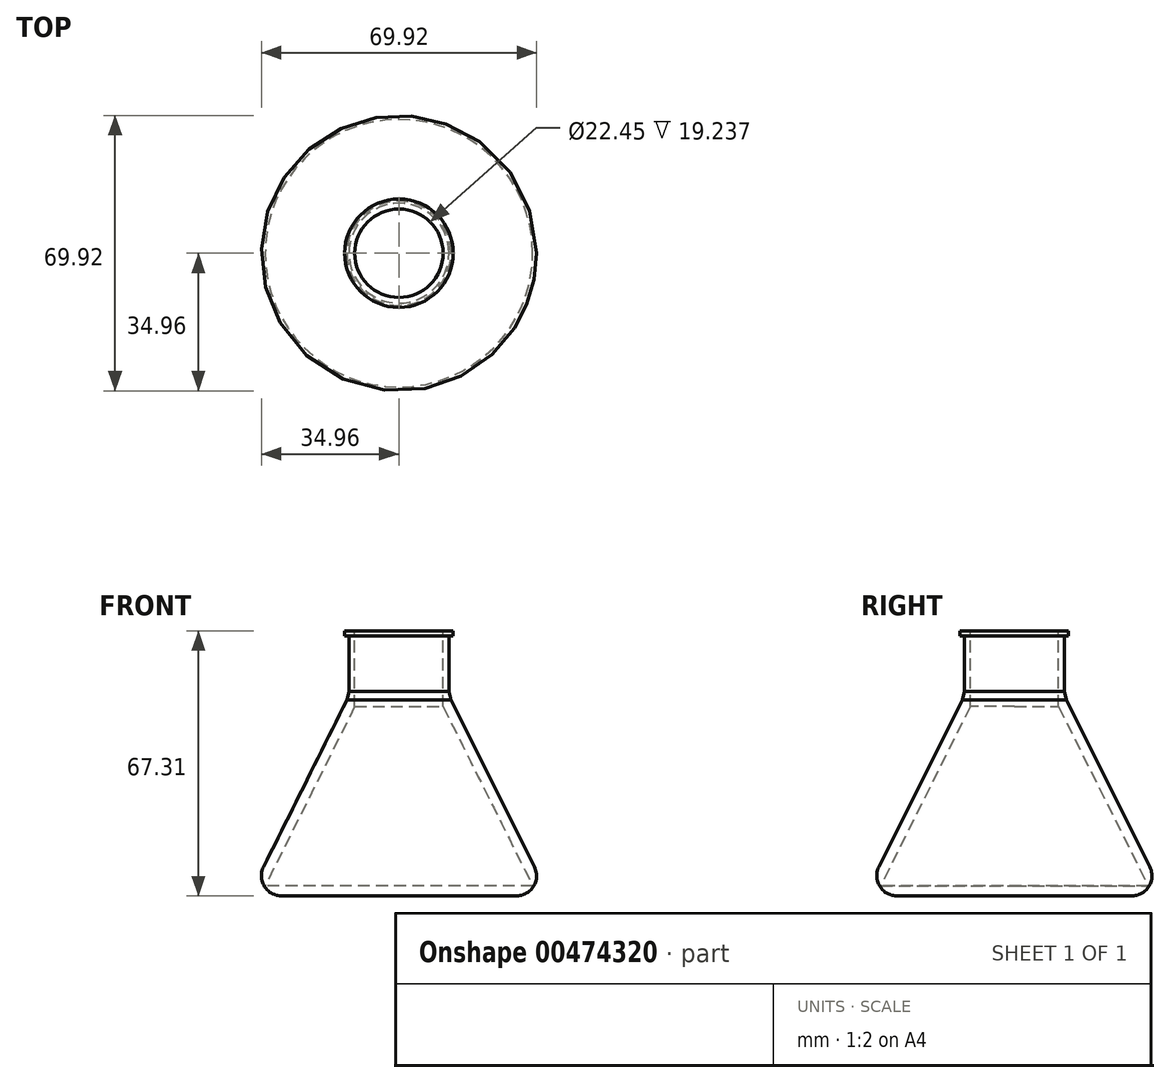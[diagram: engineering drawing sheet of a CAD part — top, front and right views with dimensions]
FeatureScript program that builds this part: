
annotation { "Feature Type Name" : "Feature", "Feature Type Description" : "" }
export const myFeature = defineFeature(function(context is Context, id is Id, definition is map)
    precondition{}
    {
        {
            var Q0;
            Q0=qCreatedBy(makeId("Top.planeOp"),FACE);
            var sketch = newSketch(context, id + "F0", { "sketchPlane" : qUnion([Q0])});
            skCircle(sketch, "E0", {"center": v(0, 0) * mm, "radius": 38.1 * mm});
            skSolve(sketch);
        }
        {
            var Q0;
            Q0=qCreatedBy(makeId("Top.planeOp"),FACE);
            cPlane(context, id + "F1", {"entities" : qUnion([Q0]), "cplaneType" : CPlaneType.OFFSET, "offset" : 50.8 * mm, "width" : 152.4 * mm, "height" : 152.4 * mm});
        }
        {
            var Q0;
            Q0=qCreatedBy(id+"F1.planeOp",FACE);
            var sketch = newSketch(context, id + "F2", { "sketchPlane" : qUnion([Q0])});
            skCircle(sketch, "E1", {"center": v(0, 0) * mm, "radius": 12.7 * mm});
            skSolve(sketch);
        }
        {
            var Q0;
            Q0=makeQuery(id+"F0.imprint","IMPRINT",FACE,{"disambiguationData":[TD([[makeQuery(id+"F0.imprint","IMPRINT",EDGE,{"derivedFrom":sQuery(id+"F0.wireOp",EDGE,"E0")}),1.0]])]});
            var Q1;
            Q1=makeQuery(id+"F2.imprint","IMPRINT",FACE,{"disambiguationData":[TD([[makeQuery(id+"F2.imprint","IMPRINT",EDGE,{"derivedFrom":sQuery(id+"F2.wireOp",EDGE,"E1")}),1.0]])]});
            loft(context, id + "F3", {"sheetProfilesArray" : [{ "sheetProfileEntities" : qUnion([Q0]) }, { "sheetProfileEntities" : qUnion([Q1]) }]});
        }
        {
            var Q0;
            Q0=makeQuery(id+"F3.opLoft","CAP_FACE",FACE,{"disambiguationData":[OSD([makeQuery(id+"F2.imprint","IMPRINT",FACE,{"disambiguationData":[TD([[makeQuery(id+"F2.imprint","IMPRINT",EDGE,{"derivedFrom":sQuery(id+"F2.wireOp",EDGE,"E1")}),1.0]])]})])],"isStart":true});
            shell(context, id + "F4", {"entities" : qUnion([Q0]), "thickness" : 2.54 * mm});
        }
        {
            var Q0;
            Q0=qCreatedBy(id+"F1.planeOp",FACE);
            var sketch = newSketch(context, id + "F5", { "sketchPlane" : qUnion([Q0])});
            skCircle(sketch, "E2", {"center": v(0, 0) * mm, "radius": 12.7 * mm});
            skSolve(sketch);
        }
        {
            var Q0;
            Q0 = qSketchRegion(id + "F5", true);
            extrude(context, id + "F6", {"entities" : qUnion([Q0]), "operationType" : NewBodyOperationType.ADD, "depth" : 15.24 * mm});
        }
        {
            var Q0;
            Q0=makeQuery(id+"F6.opExtrude","CAP_FACE",FACE,{"disambiguationData":[OSD([sQuery(id+"F5.wireOp",EDGE,"E2")])],"isStart":false});
            var sketch = newSketch(context, id + "F7", { "sketchPlane" : qUnion([Q0])});
            skCircle(sketch, "E3", {"center": v(0, 0) * mm, "radius": 10.56 * mm});
            skSolve(sketch);
        }
        {
            var Q0;
            Q0=makeQuery(id+"F7.imprint","IMPRINT",FACE,{"disambiguationData":[TD([[makeQuery(id+"F7.imprint","IMPRINT",EDGE,{"derivedFrom":sQuery(id+"F7.wireOp",EDGE,"E3")}),1.0]])]});
            extrude(context, id + "F8", {"entities" : qUnion([Q0]), "operationType" : NewBodyOperationType.REMOVE, "oppositeDirection" : true, "depth" : 53.34 * mm});
        }
        {
            var Q0;
            Q0=makeQuery(id+"F3.opLoft","MID_CAP_EDGE",EDGE,{"disambiguationData":[OSD([sQuery(id+"F0.wireOp",EDGE,"E0")])],"capPos":0.0});
            fillet(context, id + "F9", {"entities" : qUnion([Q0]), "radius" : 5.08 * mm, "tangentPropagation" : true, "allowEdgeOverflow" : false});
        }
        {
            var Q0;
            Q0=makeQuery(id+"F6.boolean.opBoolean","MERGE",EDGE,{"derivedFrom":[makeQuery(id+"F3.opLoft","MID_CAP_EDGE",EDGE,{"disambiguationData":[OSD([sQuery(id+"F0.wireOp",EDGE,"E0"),sQuery(id+"F2.wireOp",EDGE,"E1")])],"capPos":1.0}),makeQuery(id+"F6.opExtrude","CAP_EDGE",EDGE,{"disambiguationData":[OSD([sQuery(id+"F5.wireOp",EDGE,"E2")])],"isStart":true})]});
            chamfer(context, id + "F10", {"entities" : qUnion([Q0]), "width" : 5.08 * mm, "tangentPropagation" : true});
        }
        {
            var Q0;
            Q0=makeQuery(id+"F6.opExtrude","CAP_FACE",FACE,{"disambiguationData":[OSD([sQuery(id+"F5.wireOp",EDGE,"E2")])],"isStart":false});
            var sketch = newSketch(context, id + "F11", { "sketchPlane" : qUnion([Q0])});
            skCircle(sketch, "E4", {"center": v(0, 0) * mm, "radius": 13.78 * mm});
            skSolve(sketch);
        }
        {
            var Q0;
            Q0 = qSketchRegion(id + "F11", true);
            extrude(context, id + "F12", {"entities" : qUnion([Q0]), "operationType" : NewBodyOperationType.ADD, "depth" : 1.27 * mm});
        }
        {
            var Q0;
            Q0=makeQuery(id+"F12.opExtrude","CAP_FACE",FACE,{"disambiguationData":[OSD([sQuery(id+"F11.wireOp",EDGE,"E4")])],"isStart":false});
            var sketch = newSketch(context, id + "F13", { "sketchPlane" : qUnion([Q0])});
            skCircle(sketch, "E5", {"center": v(0, 0) * mm, "radius": 11.22 * mm});
            skSolve(sketch);
        }
        {
            var Q0;
            Q0=makeQuery(id+"F13.imprint","IMPRINT",FACE,{"disambiguationData":[TD([[makeQuery(id+"F13.imprint","IMPRINT",EDGE,{"derivedFrom":sQuery(id+"F13.wireOp",EDGE,"E5")}),1.0]])]});
            extrude(context, id + "F14", {"entities" : qUnion([Q0]), "operationType" : NewBodyOperationType.REMOVE, "oppositeDirection" : true, "depth" : 101.6 * mm});
        }
        {
            var Q0;
            Q0=makeQuery(id+"F0.imprint","IMPRINT",FACE,{"disambiguationData":[TD([[makeQuery(id+"F0.imprint","IMPRINT",EDGE,{"derivedFrom":sQuery(id+"F0.wireOp",EDGE,"E0")}),1.0]])]});
            cPlane(context, id + "F15", {"entities" : qUnion([Q0]), "cplaneType" : CPlaneType.OFFSET, "offset" : 0 * mm, "width" : 152.4 * mm, "height" : 152.4 * mm});
        }
        {
            var Q0;
            Q0=qCreatedBy(id+"F15.planeOp",FACE);
            var sketch = newSketch(context, id + "F16", { "sketchPlane" : qUnion([Q0])});
            skCircle(sketch, "E6.0", {"center": v(0, 0) * mm, "radius": 11.22 * mm});
            skSolve(sketch);
        }
        {
            var Q0;
            Q0=makeQuery(id+"F16.imprint","IMPRINT",FACE,{"disambiguationData":[TD([[makeQuery(id+"F16.imprint","IMPRINT",EDGE,{"derivedFrom":sQuery(id+"F16.wireOp",EDGE,"E6.0")}),1.0]])]});
            extrude(context, id + "F17", {"entities" : qUnion([Q0]), "operationType" : NewBodyOperationType.ADD, "depth" : 2.54 * mm});
        }
    });
